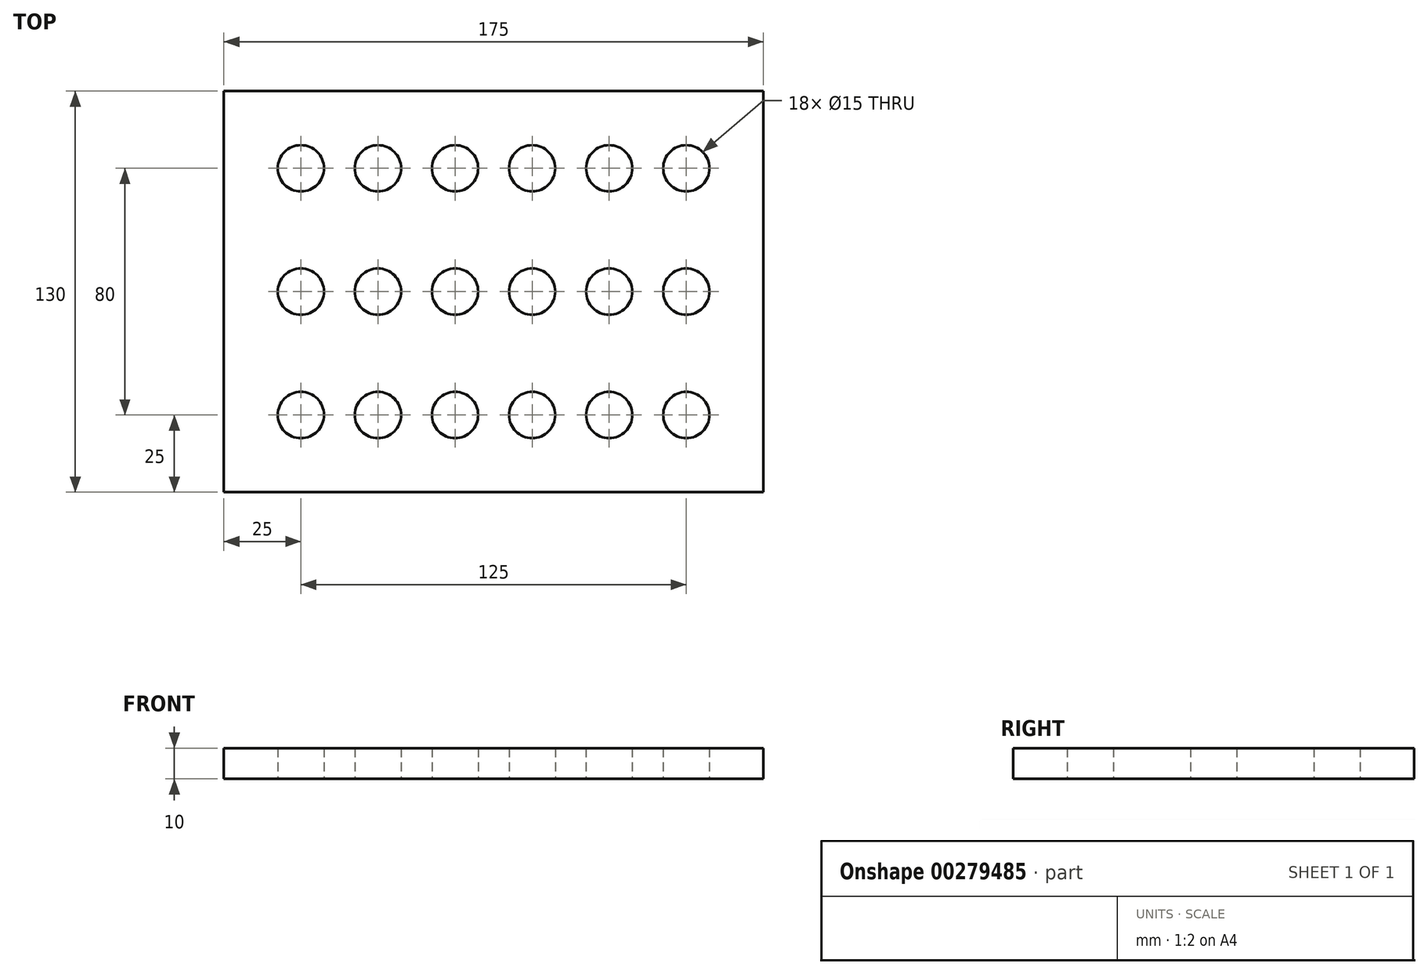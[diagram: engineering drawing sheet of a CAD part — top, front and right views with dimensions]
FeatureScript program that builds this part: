
annotation { "Feature Type Name" : "Feature", "Feature Type Description" : "" }
export const myFeature = defineFeature(function(context is Context, id is Id, definition is map)
    precondition{}
    {
        {
            var Q0;
            Q0=qCreatedBy(makeId("Top.planeOp"),FACE);
            var sketch = newSketch(context, id + "F0", { "sketchPlane" : qUnion([Q0])});
            skPoint(sketch, "E0.middle", {"position": v(0, 0) * mm});
            skLineSegment(sketch, "E1.bottom", {"start": v(87.5, -65) * mm, "end": v(-87.5, -65) * mm});
            skLineSegment(sketch, "E1.top", {"start": v(87.5, 65) * mm, "end": v(-87.5, 65) * mm});
            skLineSegment(sketch, "E1.left", {"start": v(87.5, -65) * mm, "end": v(87.5, 65) * mm});
            skLineSegment(sketch, "E1.right", {"start": v(-87.5, -65) * mm, "end": v(-87.5, 65) * mm});
            skCircle(sketch, "E2", {"center": v(-62.5, 40) * mm, "radius": 7.5 * mm});
            skCircle(sketch, "E3.0.1.0", {"center": v(-62.5, 0) * mm, "radius": 7.5 * mm});
            skCircle(sketch, "E3.0.2.0", {"center": v(-62.5, -40) * mm, "radius": 7.5 * mm});
            skCircle(sketch, "E3.1.0.0", {"center": v(-37.5, 40) * mm, "radius": 7.5 * mm});
            skCircle(sketch, "E3.1.1.0", {"center": v(-37.5, 0) * mm, "radius": 7.5 * mm});
            skCircle(sketch, "E3.1.2.0", {"center": v(-37.5, -40) * mm, "radius": 7.5 * mm});
            skCircle(sketch, "E3.2.0.0", {"center": v(-12.5, 40) * mm, "radius": 7.5 * mm});
            skCircle(sketch, "E3.2.1.0", {"center": v(-12.5, 0) * mm, "radius": 7.5 * mm});
            skCircle(sketch, "E3.2.2.0", {"center": v(-12.5, -40) * mm, "radius": 7.5 * mm});
            skCircle(sketch, "E3.3.0.0", {"center": v(12.5, 40) * mm, "radius": 7.5 * mm});
            skCircle(sketch, "E3.3.1.0", {"center": v(12.5, 0) * mm, "radius": 7.5 * mm});
            skCircle(sketch, "E3.3.2.0", {"center": v(12.5, -40) * mm, "radius": 7.5 * mm});
            skCircle(sketch, "E3.4.0.0", {"center": v(37.5, 40) * mm, "radius": 7.5 * mm});
            skCircle(sketch, "E3.4.1.0", {"center": v(37.5, 0) * mm, "radius": 7.5 * mm});
            skCircle(sketch, "E3.4.2.0", {"center": v(37.5, -40) * mm, "radius": 7.5 * mm});
            skCircle(sketch, "E3.5.0.0", {"center": v(62.5, 40) * mm, "radius": 7.5 * mm});
            skCircle(sketch, "E3.5.1.0", {"center": v(62.5, 0) * mm, "radius": 7.5 * mm});
            skCircle(sketch, "E3.5.2.0", {"center": v(62.5, -40) * mm, "radius": 7.5 * mm});
            skLineSegment(sketch, "E3.direction1", {"start": v(-62.5, 40) * mm, "end": v(-37.5, 40) * mm, "construction": true});
            skLineSegment(sketch, "E3.direction2", {"start": v(-62.5, 40) * mm, "end": v(-62.5, 0) * mm, "construction": true});
            skSolve(sketch);
        }
        {
            var Q0;
            Q0 = qSketchRegion(id + "F0", true);
            extrude(context, id + "F1", {"entities" : qUnion([Q0]), "depth" : 10 * mm});
        }
    });
